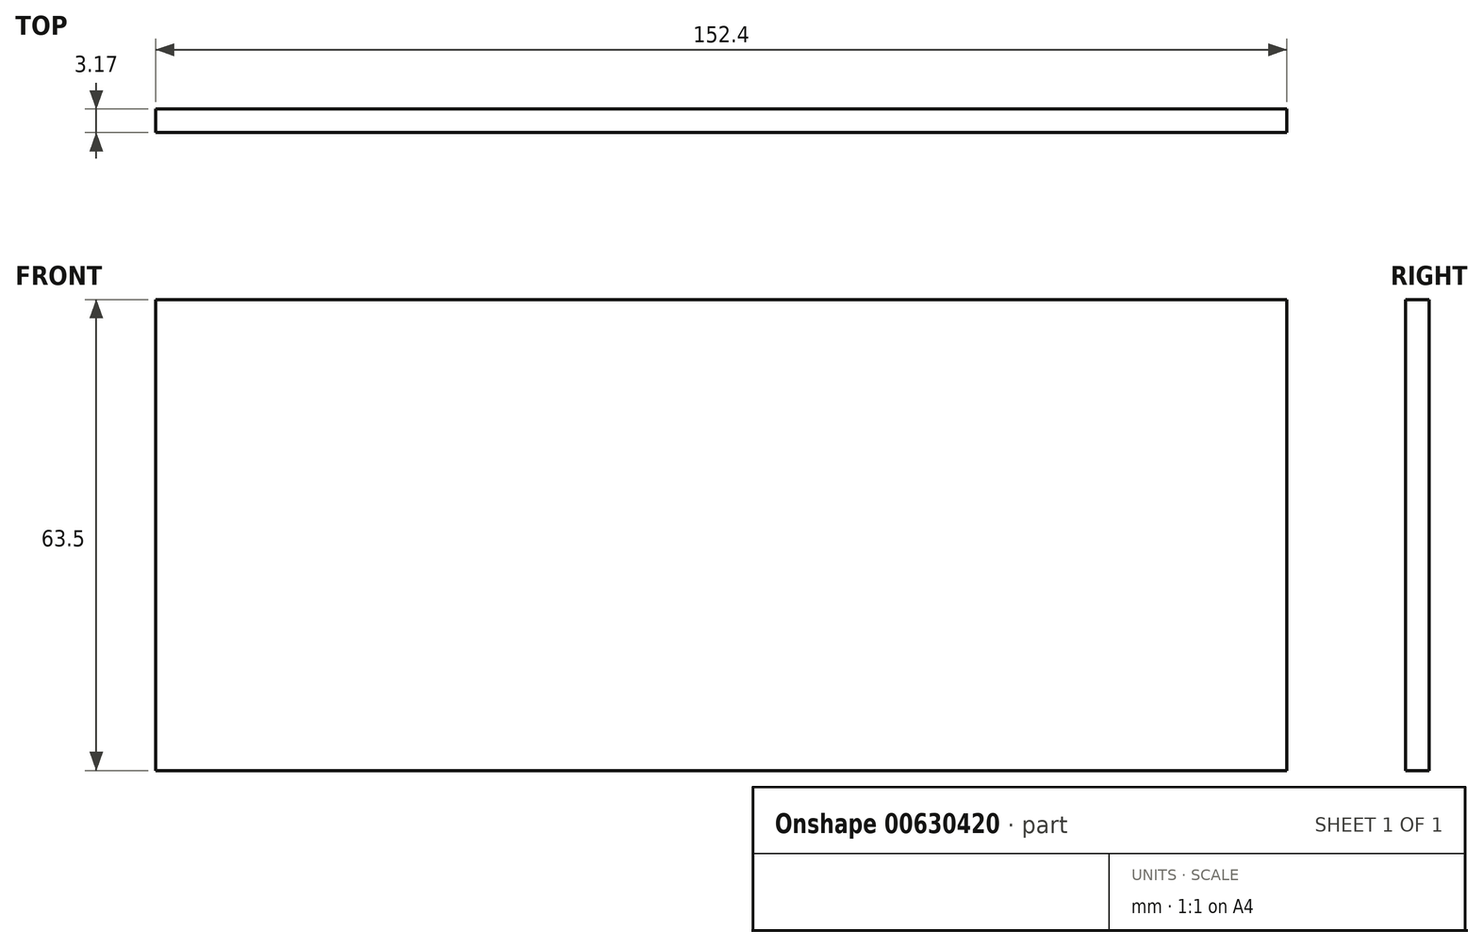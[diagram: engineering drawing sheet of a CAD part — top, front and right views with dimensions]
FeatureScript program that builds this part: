
annotation { "Feature Type Name" : "Feature", "Feature Type Description" : "" }
export const myFeature = defineFeature(function(context is Context, id is Id, definition is map)
    precondition{}
    {
        {
            var Q0;
            Q0=qCreatedBy(makeId("Front.planeOp"),FACE);
            var sketch = newSketch(context, id + "F0", { "sketchPlane" : qUnion([Q0])});
            skLineSegment(sketch, "E0.bottom", {"start": v(76.2, 31.75) * mm, "end": v(-76.2, 31.75) * mm});
            skLineSegment(sketch, "E0.top", {"start": v(76.2, -31.75) * mm, "end": v(-76.2, -31.75) * mm});
            skLineSegment(sketch, "E0.left", {"start": v(76.2, 31.75) * mm, "end": v(76.2, -31.75) * mm});
            skLineSegment(sketch, "E0.right", {"start": v(-76.2, 31.75) * mm, "end": v(-76.2, -31.75) * mm});
            skPoint(sketch, "E0.middle", {"position": v(0, 0) * mm});
            skSolve(sketch);
        }
        {
            var Q0;
            Q0=makeQuery(id+"F0.imprint","IMPRINT",FACE,{"disambiguationData":[TD([[makeQuery(id+"F0.imprint","IMPRINT",EDGE,{"derivedFrom":sQuery(id+"F0.wireOp",EDGE,"E0.bottom")}),1.0]])]});
            extrude(context, id + "F1", {"entities" : qUnion([Q0]), "depth" : 3.17 * mm, "offsetDistance" : 25.4 * mm});
        }
    });
